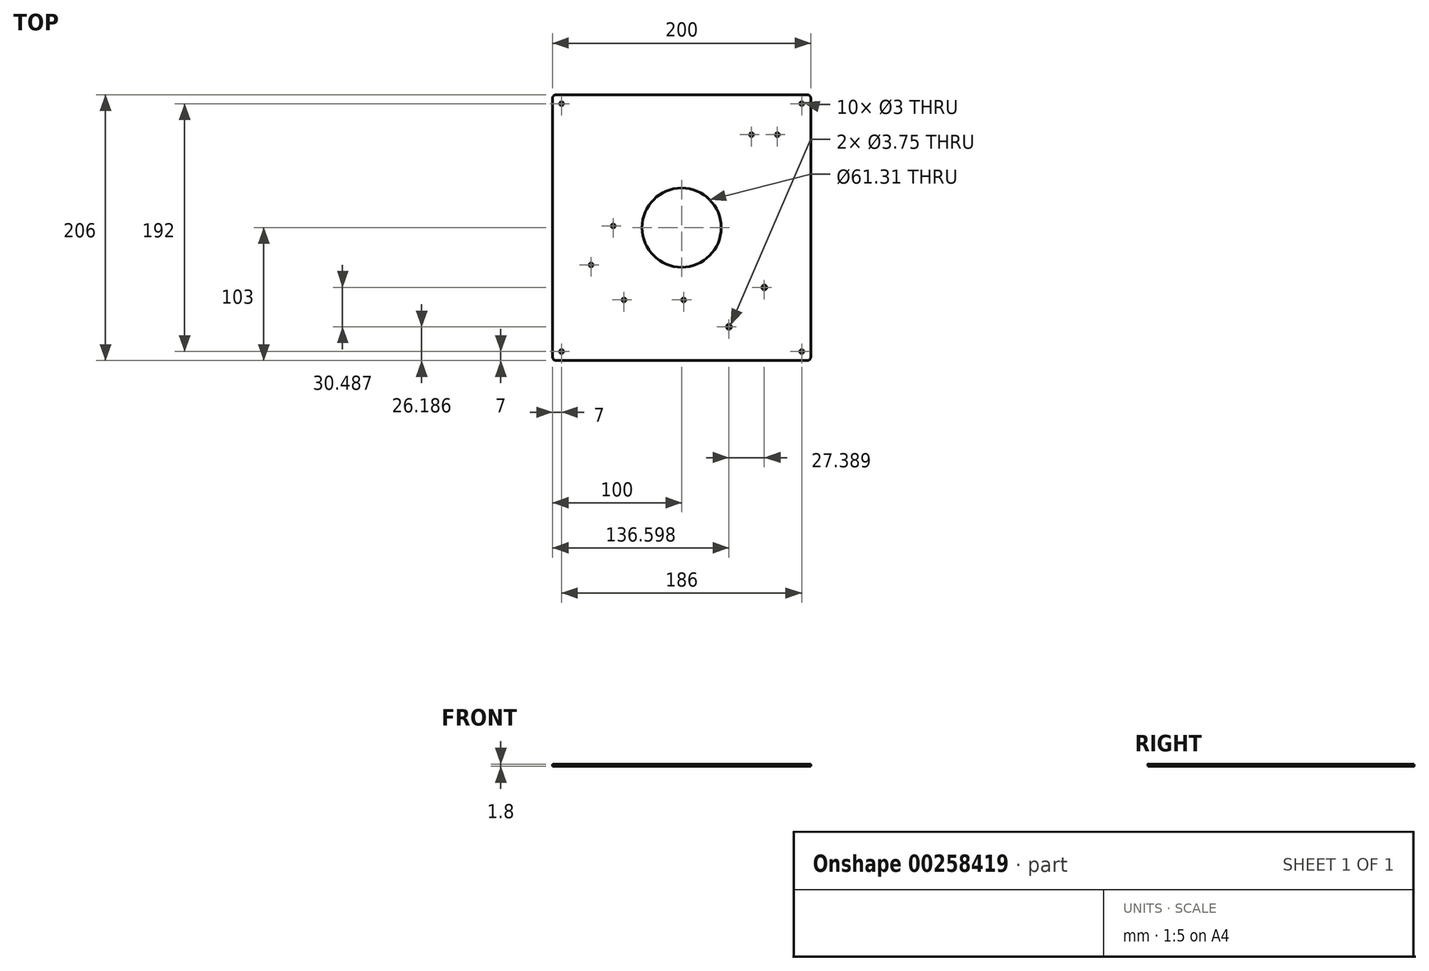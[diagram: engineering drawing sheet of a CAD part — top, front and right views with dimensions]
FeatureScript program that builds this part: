
annotation { "Feature Type Name" : "Feature", "Feature Type Description" : "" }
export const myFeature = defineFeature(function(context is Context, id is Id, definition is map)
    precondition{}
    {
        {
            var Q0;
            Q0=qCreatedBy(makeId("Top.planeOp"),FACE);
            var sketch = newSketch(context, id + "F0", { "sketchPlane" : qUnion([Q0])});
            skLineSegment(sketch, "E0.bottom", {"start": v(97, -103) * mm, "end": v(-97, -103) * mm});
            skLineSegment(sketch, "E0.top", {"start": v(97, 103) * mm, "end": v(-97, 103) * mm});
            skLineSegment(sketch, "E0.left", {"start": v(100, -100) * mm, "end": v(100, 100) * mm});
            skLineSegment(sketch, "E0.right", {"start": v(-100, -100) * mm, "end": v(-100, 100) * mm});
            skCircle(sketch, "E1", {"center": v(-44.68, -55.97) * mm, "radius": 1.5 * mm});
            skCircle(sketch, "E2", {"center": v(1.53, -55.97) * mm, "radius": 1.5 * mm});
            skPoint(sketch, "E3.visualSharp", {"position": v(-100, 103) * mm});
            skArc(sketch, "E3.filletArc", {"start": v(-97, 103) * mm, "mid": v(-99.12, 102.12) * mm, "end": v(-100, 100) * mm});
            skPoint(sketch, "E4.visualSharp", {"position": v(100, 103) * mm});
            skArc(sketch, "E4.filletArc", {"start": v(100, 100) * mm, "mid": v(99.12, 102.12) * mm, "end": v(97, 103) * mm});
            skPoint(sketch, "E5.visualSharp", {"position": v(100, -103) * mm});
            skArc(sketch, "E5.filletArc", {"start": v(97, -103) * mm, "mid": v(99.12, -102.12) * mm, "end": v(100, -100) * mm});
            skPoint(sketch, "E6.visualSharp", {"position": v(-100, -103) * mm});
            skArc(sketch, "E6.filletArc", {"start": v(-100, -100) * mm, "mid": v(-99.12, -102.12) * mm, "end": v(-97, -103) * mm});
            skCircle(sketch, "E7.MirrorC", {"center": v(93, 96) * mm, "radius": 1.5 * mm});
            skCircle(sketch, "E8", {"center": v(63.99, -46.33) * mm, "radius": 1.88 * mm});
            skCircle(sketch, "E9", {"center": v(36.6, -76.81) * mm, "radius": 1.88 * mm});
            skPoint(sketch, "E10.middle", {"position": v(-61.57, -13.8) * mm});
            skCircle(sketch, "E11", {"center": v(-52.97, 1.3) * mm, "radius": 1.5 * mm});
            skCircle(sketch, "E12.MirrorC", {"center": v(-70.17, -28.9) * mm, "radius": 1.5 * mm});
            skLineSegment(sketch, "E13", {"start": v(0, 103) * mm, "end": v(0, -103) * mm, "construction": true});
            skLineSegment(sketch, "E14", {"start": v(-100, 0) * mm, "end": v(100, 0) * mm, "construction": true});
            skCircle(sketch, "E15", {"center": v(0, 0) * mm, "radius": 30.66 * mm});
            skCircle(sketch, "E16", {"center": v(74.08, 72) * mm, "radius": 1.5 * mm});
            skCircle(sketch, "E17", {"center": v(54.08, 72) * mm, "radius": 1.5 * mm});
            skCircle(sketch, "E18.MirrorC", {"center": v(-93, 96) * mm, "radius": 1.5 * mm});
            skCircle(sketch, "E19.MirrorC", {"center": v(93, -96) * mm, "radius": 1.5 * mm});
            skCircle(sketch, "E20.MirrorC", {"center": v(-93, -96) * mm, "radius": 1.5 * mm});
            skSolve(sketch);
        }
        {
            var Q0;
            Q0=makeQuery(id+"F0.imprint","IMPRINT",FACE,{"disambiguationData":[TD([[makeQuery(id+"F0.imprint","IMPRINT",EDGE,{"derivedFrom":sQuery(id+"F0.wireOp",EDGE,"E0.bottom")}),-1.0]])]});
            extrude(context, id + "F1", {"entities" : qUnion([Q0]), "depth" : 1.8 * mm});
        }
    });
